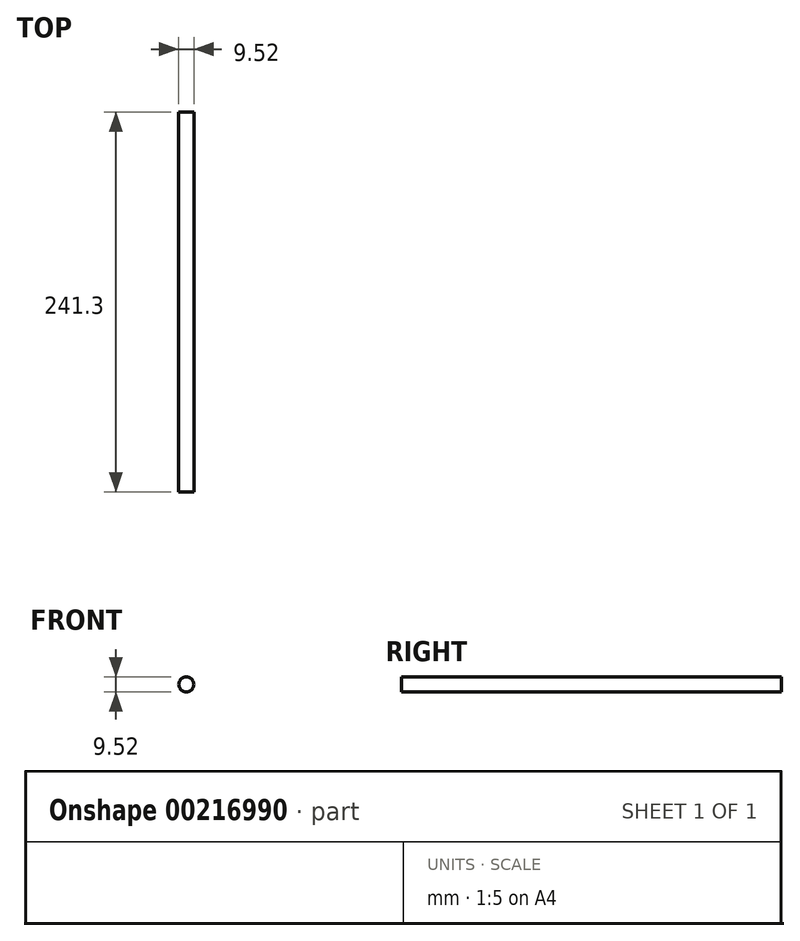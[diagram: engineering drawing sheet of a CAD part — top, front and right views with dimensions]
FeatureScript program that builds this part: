
annotation { "Feature Type Name" : "Feature", "Feature Type Description" : "" }
export const myFeature = defineFeature(function(context is Context, id is Id, definition is map)
    precondition{}
    {
        {
            var Q0;
            Q0=qCreatedBy(makeId("Front.planeOp"),FACE);
            var sketch = newSketch(context, id + "F0", { "sketchPlane" : qUnion([Q0])});
            skCircle(sketch, "E0", {"center": v(0, 0) * mm, "radius": 4.76 * mm});
            skSolve(sketch);
        }
        {
            var Q0;
            Q0=makeQuery(id+"F0.imprint","IMPRINT",FACE,{"disambiguationData":[TD([[makeQuery(id+"F0.imprint","IMPRINT",EDGE,{"derivedFrom":sQuery(id+"F0.wireOp",EDGE,"E0")}),1.0]])]});
            extrude(context, id + "F1", {"entities" : qUnion([Q0]), "depth" : 241.3 * mm});
        }
    });
